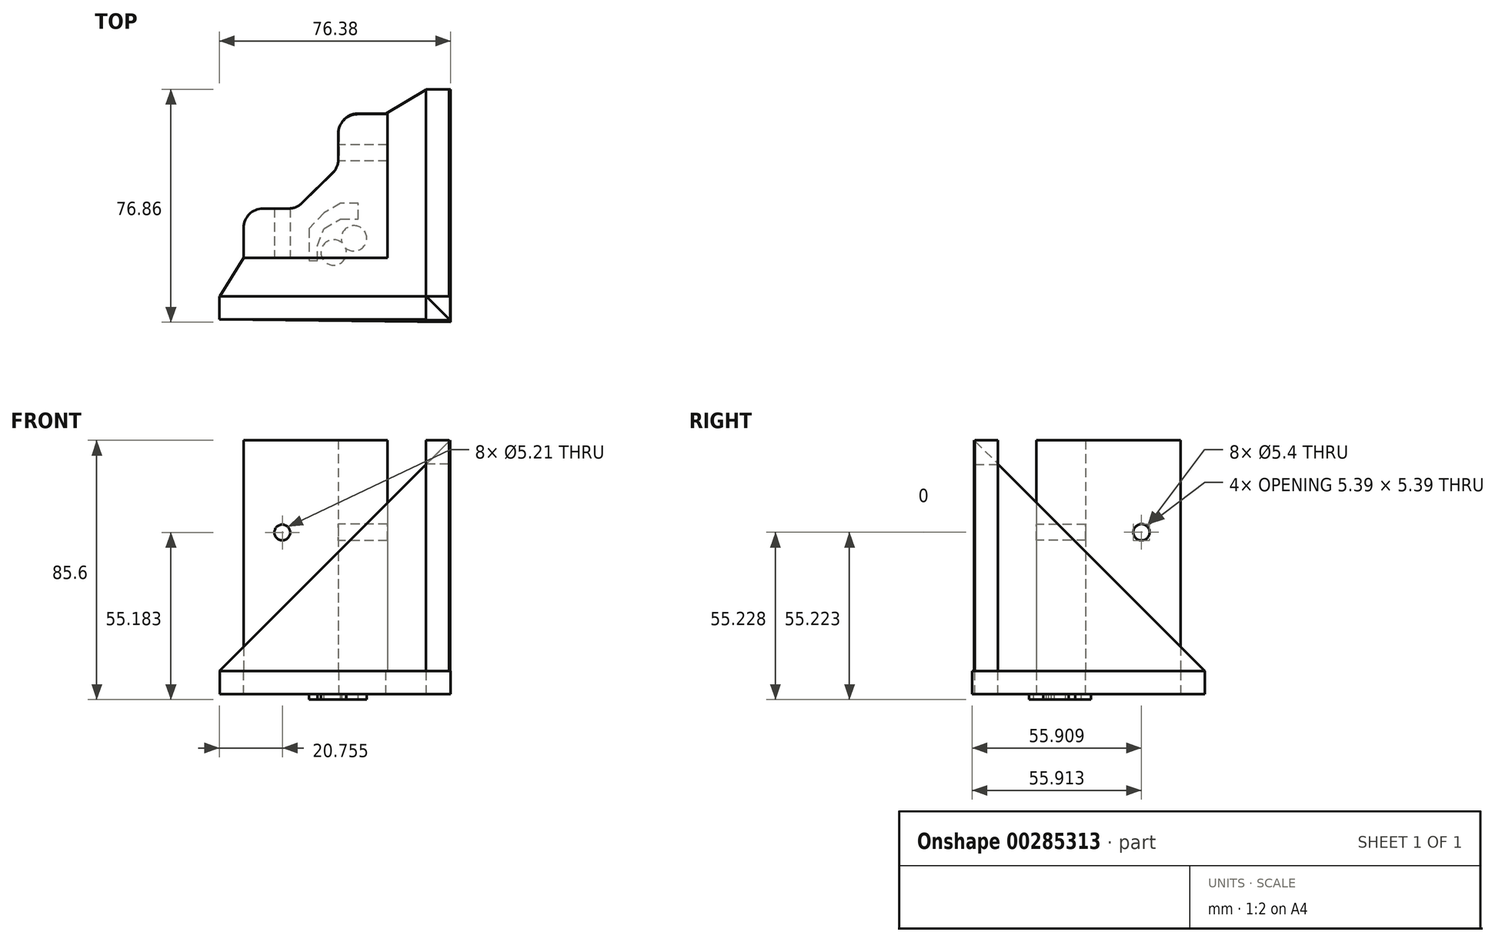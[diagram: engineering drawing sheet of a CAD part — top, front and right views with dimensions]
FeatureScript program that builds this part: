
annotation { "Feature Type Name" : "Feature", "Feature Type Description" : "" }
export const myFeature = defineFeature(function(context is Context, id is Id, definition is map)
    precondition{}
    {
        {
            var Q0;
            Q0=qCreatedBy(makeId("Front.planeOp"),FACE);
            var sketch = newSketch(context, id + "F0", { "sketchPlane" : qUnion([Q0])});
            skLineSegment(sketch, "E0", {"start": v(-37.72, 0) * mm, "end": v(38.48, 0) * mm});
            skLineSegment(sketch, "E1", {"start": v(38.48, 0) * mm, "end": v(38.48, 76.2) * mm});
            skLineSegment(sketch, "E2", {"start": v(-37.72, 0) * mm, "end": v(38.48, 76.2) * mm});
            skSolve(sketch);
        }
        {
            var Q0;
            Q0 = qSketchRegion(id + "F0", true);
            var Q1;
            Q1 = qSketchRegion(id + "F2", true);
            extrude(context, id + "F1", {"entities" : qUnion([Q0, Q1]), "depth" : 7.62 * mm});
        }
        {
            var Q0;
            Q0=qCreatedBy(makeId("Right.planeOp"),FACE);
            var sketch = newSketch(context, id + "F2", { "sketchPlane" : qUnion([Q0])});
            skLineSegment(sketch, "E3", {"start": v(-7.9, 76.2) * mm, "end": v(-7.9, 0) * mm});
            skLineSegment(sketch, "E4", {"start": v(-7.9, 76.2) * mm, "end": v(68.3, 0) * mm});
            skLineSegment(sketch, "E5", {"start": v(68.3, 0) * mm, "end": v(-7.9, 0) * mm});
            skSolve(sketch);
        }
        {
            var Q0;
            Q0 = qSketchRegion(id + "F2", true);
            extrude(context, id + "F3", {"entities" : qUnion([Q0]), "operationType" : NewBodyOperationType.ADD, "depth" : 38.1 * mm, "hasSecondDirection" : true, "secondDirectionOppositeDirection" : false, "secondDirectionDepth" : 30.48 * mm});
        }
        {
            var Q0;
            Q0=qCreatedBy(makeId("Top.planeOp"),FACE);
            var sketch = newSketch(context, id + "F4", { "sketchPlane" : qUnion([Q0])});
            skLineSegment(sketch, "E6", {"start": v(17.78, 60.2) * mm, "end": v(17.78, 12.7) * mm});
            skLineSegment(sketch, "E7", {"start": v(17.78, 12.7) * mm, "end": v(-29.73, 12.7) * mm});
            skLineSegment(sketch, "E8", {"start": v(-29.73, 12.7) * mm, "end": v(-29.73, 22.6) * mm});
            skLineSegment(sketch, "E9", {"start": v(-23.38, 28.94) * mm, "end": v(-14.87, 28.94) * mm});
            skLineSegment(sketch, "E10", {"start": v(-10.42, 30.76) * mm, "end": v(-0.36, 40.65) * mm});
            skLineSegment(sketch, "E11", {"start": v(1.54, 45.18) * mm, "end": v(1.54, 53.71) * mm});
            skLineSegment(sketch, "E12", {"start": v(7.8, 60.06) * mm, "end": v(17.78, 60.2) * mm});
            skPoint(sketch, "E13.visualSharp", {"position": v(-29.73, 28.94) * mm});
            skArc(sketch, "E13.filletArc", {"start": v(-23.38, 28.94) * mm, "mid": v(-27.87, 27.08) * mm, "end": v(-29.73, 22.6) * mm});
            skPoint(sketch, "E14.visualSharp", {"position": v(1.54, 59.97) * mm});
            skArc(sketch, "E14.filletArc", {"start": v(7.8, 60.06) * mm, "mid": v(3.37, 58.17) * mm, "end": v(1.54, 53.71) * mm});
            skPoint(sketch, "E15.visualSharp", {"position": v(1.54, 42.52) * mm});
            skArc(sketch, "E15.filletArc", {"start": v(-0.36, 40.65) * mm, "mid": v(1.05, 42.73) * mm, "end": v(1.54, 45.18) * mm});
            skPoint(sketch, "E16.visualSharp", {"position": v(-12.28, 28.94) * mm});
            skArc(sketch, "E16.filletArc", {"start": v(-14.87, 28.94) * mm, "mid": v(-12.47, 29.41) * mm, "end": v(-10.42, 30.76) * mm});
            skSolve(sketch);
        }
        {
            var Q0;
            Q0 = qSketchRegion(id + "F4", true);
            extrude(context, id + "F5", {"entities" : qUnion([Q0]), "depth" : 76.2 * mm});
        }
        {
            var Q0;
            Q0=qCreatedBy(makeId("Top.planeOp"),FACE);
            var sketch = newSketch(context, id + "F6", { "sketchPlane" : qUnion([Q0])});
            skLineSegment(sketch, "E17", {"start": v(-29.67, 12.78) * mm, "end": v(-37.54, 0) * mm});
            skPoint(sketch, "E18.endSnap0", {"position": v(-37.54, -2.9) * mm});
            skLineSegment(sketch, "E19", {"start": v(38.66, -8.56) * mm, "end": v(38.66, 67.64) * mm});
            skLineSegment(sketch, "E20", {"start": v(-17.69, 28.84) * mm, "end": v(-23.32, 28.84) * mm});
            skLineSegment(sketch, "E21", {"start": v(-29.67, 22.49) * mm, "end": v(-29.67, 12.78) * mm});
            skLineSegment(sketch, "E22", {"start": v(-37.54, 0) * mm, "end": v(-37.54, -7.62) * mm});
            skLineSegment(sketch, "E23", {"start": v(-37.54, -7.62) * mm, "end": v(38.66, -8.56) * mm});
            skLineSegment(sketch, "E24", {"start": v(17.31, 60.33) * mm, "end": v(8.06, 60.33) * mm});
            skLineSegment(sketch, "E25", {"start": v(1.71, 53.98) * mm, "end": v(1.71, 45.43) * mm});
            skLineSegment(sketch, "E26", {"start": v(-0.17, 40.91) * mm, "end": v(-10.52, 30.67) * mm});
            skLineSegment(sketch, "E27", {"start": v(-15, 28.83) * mm, "end": v(-17.69, 28.84) * mm});
            skLineSegment(sketch, "E28", {"start": v(17.31, 60.33) * mm, "end": v(30.66, 68.28) * mm});
            skLineSegment(sketch, "E29", {"start": v(30.66, 68.28) * mm, "end": v(38.66, 68.28) * mm});
            skLineSegment(sketch, "E30", {"start": v(38.66, 68.28) * mm, "end": v(38.66, 67.64) * mm});
            skPoint(sketch, "E31.visualSharp", {"position": v(-29.67, 28.84) * mm});
            skArc(sketch, "E31.filletArc", {"start": v(-23.32, 28.84) * mm, "mid": v(-27.8, 26.98) * mm, "end": v(-29.67, 22.49) * mm});
            skPoint(sketch, "E32.visualSharp", {"position": v(1.71, 60.33) * mm});
            skArc(sketch, "E32.filletArc", {"start": v(8.06, 60.33) * mm, "mid": v(3.57, 58.47) * mm, "end": v(1.71, 53.98) * mm});
            skPoint(sketch, "E33.visualSharp", {"position": v(-12.38, 28.83) * mm});
            skArc(sketch, "E33.filletArc", {"start": v(-15, 28.83) * mm, "mid": v(-12.58, 29.3) * mm, "end": v(-10.52, 30.67) * mm});
            skPoint(sketch, "E34.visualSharp", {"position": v(1.71, 42.78) * mm});
            skArc(sketch, "E34.filletArc", {"start": v(-0.17, 40.91) * mm, "mid": v(1.22, 42.98) * mm, "end": v(1.71, 45.43) * mm});
            skSolve(sketch);
        }
        {
            var Q0;
            Q0 = qSketchRegion(id + "F6", true);
            extrude(context, id + "F7", {"entities" : qUnion([Q0]), "oppositeDirection" : true, "depth" : 7.62 * mm});
        }
        {
            var Q0;
            Q0=qCreatedBy(makeId("Front.planeOp"),FACE);
            var sketch = newSketch(context, id + "F8", { "sketchPlane" : qUnion([Q0])});
            skCircle(sketch, "E35", {"center": v(-16.96, 45.78) * mm, "radius": 2.6 * mm});
            skSolve(sketch);
        }
        {
            var Q0;
            Q0 = qSketchRegion(id + "F8", true);
            extrude(context, id + "F9", {"entities" : qUnion([Q0]), "operationType" : NewBodyOperationType.REMOVE, "oppositeDirection" : true, "depth" : 98.8 * mm});
        }
        {
            var Q0;
            Q0=qCreatedBy(makeId("Right.planeOp"),FACE);
            var sketch = newSketch(context, id + "F10", { "sketchPlane" : qUnion([Q0])});
            skCircle(sketch, "E36", {"center": v(47.35, 45.83) * mm, "radius": 2.7 * mm});
            skSolve(sketch);
        }
        {
            var Q0;
            Q0 = qSketchRegion(id + "F10", true);
            extrude(context, id + "F11", {"entities" : qUnion([Q0]), "operationType" : NewBodyOperationType.REMOVE, "depth" : 47.75 * mm, "hasSecondDirection" : true, "secondDirectionOppositeDirection" : true, "secondDirectionDepth" : 45.2 * mm});
        }
        {
            var Q0;
            Q0=makeQuery(id+"F7.opExtrude","CAP_FACE",FACE,{"disambiguationData":[OSD([sQuery(id+"F6.wireOp",EDGE,"E17"),sQuery(id+"F6.wireOp",EDGE,"E19"),sQuery(id+"F6.wireOp",EDGE,"E20"),sQuery(id+"F6.wireOp",EDGE,"E21"),sQuery(id+"F6.wireOp",EDGE,"E22"),sQuery(id+"F6.wireOp",EDGE,"E23"),sQuery(id+"F6.wireOp",EDGE,"E24"),sQuery(id+"F6.wireOp",EDGE,"E25"),sQuery(id+"F6.wireOp",EDGE,"E26"),sQuery(id+"F6.wireOp",EDGE,"E27"),sQuery(id+"F6.wireOp",EDGE,"E28"),sQuery(id+"F6.wireOp",EDGE,"E29"),sQuery(id+"F6.wireOp",EDGE,"E30"),sQuery(id+"F6.wireOp",EDGE,"E31.filletArc"),sQuery(id+"F6.wireOp",EDGE,"E32.filletArc"),sQuery(id+"F6.wireOp",EDGE,"E33.filletArc"),sQuery(id+"F6.wireOp",EDGE,"E34.filletArc")])],"isStart":false});
            var sketch = newSketch(context, id + "F12", { "sketchPlane" : qUnion([Q0])});
            skLineSegment(sketch, "E37", {"start": v(-8.16, -11.8) * mm, "end": v(-5.35, -11.8) * mm});
            skPoint(sketch, "E37.endSnap0", {"position": v(-5.35, -35.8) * mm});
            skLineSegment(sketch, "E38", {"start": v(-5.35, -11.8) * mm, "end": v(-5.35, -16.76) * mm});
            skLineSegment(sketch, "E39", {"start": v(-5.35, -16.76) * mm, "end": v(-3.2, -22.3) * mm});
            skLineSegment(sketch, "E40", {"start": v(-3.2, -22.3) * mm, "end": v(2.33, -25.5) * mm});
            skLineSegment(sketch, "E41", {"start": v(2.33, -25.5) * mm, "end": v(8.16, -25.5) * mm});
            skLineSegment(sketch, "E42", {"start": v(8.16, -25.5) * mm, "end": v(8.16, -30.67) * mm});
            skLineSegment(sketch, "E43", {"start": v(8.16, -30.67) * mm, "end": v(2.33, -30.67) * mm});
            skLineSegment(sketch, "E44", {"start": v(2.33, -30.67) * mm, "end": v(-3.2, -27.54) * mm});
            skLineSegment(sketch, "E45", {"start": v(-3.2, -27.54) * mm, "end": v(-8.16, -22.3) * mm});
            skLineSegment(sketch, "E46", {"start": v(-8.16, -22.3) * mm, "end": v(-8.16, -11.8) * mm});
            skCircle(sketch, "E47", {"center": v(0, -14.43) * mm, "radius": 4.2 * mm});
            skCircle(sketch, "E48", {"center": v(6.7, -19.1) * mm, "radius": 4.2 * mm});
            skSolve(sketch);
        }
        {
            var Q0;
            Q0 = qSketchRegion(id + "F12", true);
            extrude(context, id + "F13", {"entities" : qUnion([Q0]), "operationType" : NewBodyOperationType.ADD, "depth" : 1.78 * mm});
        }
    });
